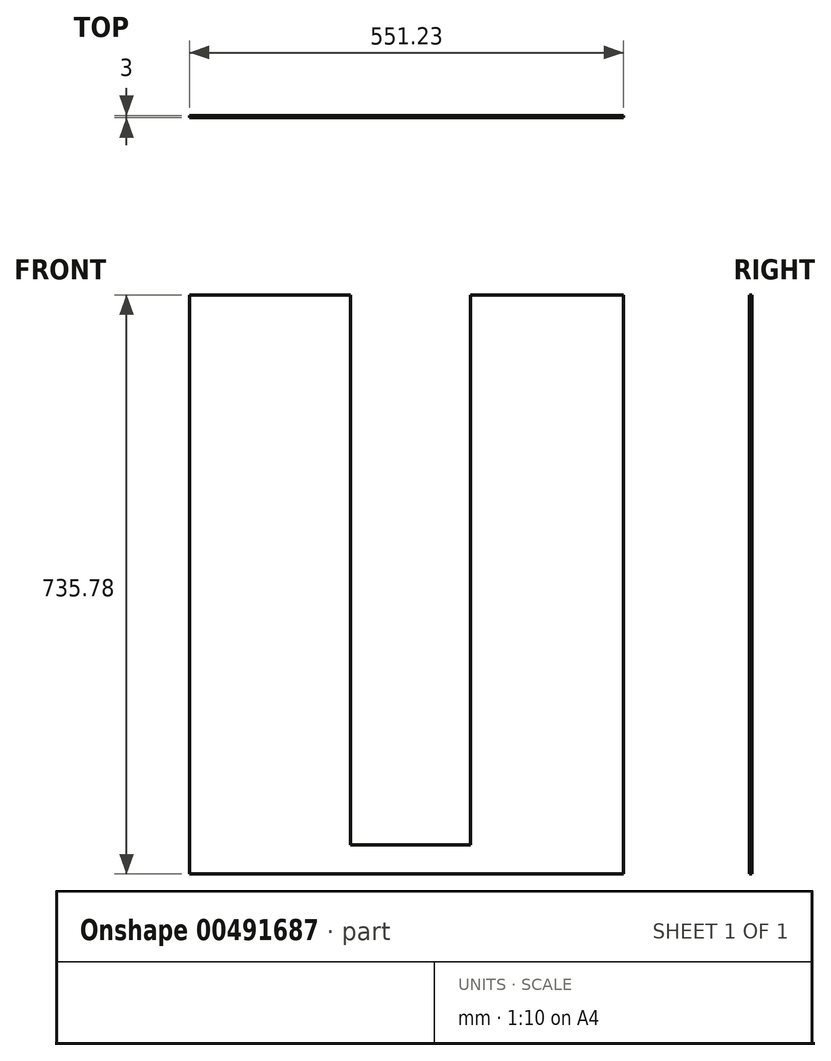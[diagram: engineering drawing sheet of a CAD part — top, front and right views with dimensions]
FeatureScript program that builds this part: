
annotation { "Feature Type Name" : "Feature", "Feature Type Description" : "" }
export const myFeature = defineFeature(function(context is Context, id is Id, definition is map)
    precondition{}
    {
        {
            var Q0;
            Q0=qCreatedBy(makeId("Front.planeOp"),FACE);
            var sketch = newSketch(context, id + "F0", { "sketchPlane" : qUnion([Q0])});
            skLineSegment(sketch, "E0.bottom", {"start": v(-280.6, 698.5) * mm, "end": v(280.6, 698.5) * mm});
            skLineSegment(sketch, "E0.top", {"start": v(-280.6, -41.27) * mm, "end": v(280.6, -41.27) * mm});
            skLineSegment(sketch, "E0.left", {"start": v(-280.6, 698.5) * mm, "end": v(-280.6, -41.27) * mm});
            skLineSegment(sketch, "E0.right", {"start": v(280.6, 698.5) * mm, "end": v(280.6, -41.27) * mm});
            skLineSegment(sketch, "E1", {"start": v(-280.6, 698.5) * mm, "end": v(0, 698.5) * mm});
            skLineSegment(sketch, "E2", {"start": v(0, 698.5) * mm, "end": v(0, 0) * mm});
            skLineSegment(sketch, "E3", {"start": v(0, 698.5) * mm, "end": v(-76.2, 698.5) * mm});
            skLineSegment(sketch, "E4", {"start": v(0, 698.5) * mm, "end": v(76.2, 698.5) * mm});
            skLineSegment(sketch, "E5", {"start": v(-76.2, 698.5) * mm, "end": v(-76.2, 0) * mm});
            skLineSegment(sketch, "E6", {"start": v(76.2, 0) * mm, "end": v(76.2, 698.5) * mm});
            skLineSegment(sketch, "E7", {"start": v(-76.2, 0) * mm, "end": v(76.2, 0) * mm});
            skSolve(sketch);
        }
        {
            var Q0;
            Q0=makeQuery(id+"F0.imprint","IMPRINT",FACE,{"disambiguationData":[TD([[makeQuery(id+"F0.imprint","IMPRINT",EDGE,{"derivedFrom":sQuery(id+"F0.wireOp",EDGE,"E0.bottom")}),-1.0]])]});
            extrude(context, id + "F1", {"entities" : qUnion([Q0]), "depth" : 3 * mm});
        }
        {
            var Q0;
            Q0=makeQuery(id+"F1.opExtrude","CAP_FACE",FACE,{"disambiguationData":[OSD([sQuery(id+"F0.wireOp",EDGE,"E0.bottom"),sQuery(id+"F0.wireOp",EDGE,"E0.top"),sQuery(id+"F0.wireOp",EDGE,"E0.left"),sQuery(id+"F0.wireOp",EDGE,"E0.right"),sQuery(id+"F0.wireOp",EDGE,"E1"),sQuery(id+"F0.wireOp",EDGE,"E5"),sQuery(id+"F0.wireOp",EDGE,"E6"),sQuery(id+"F0.wireOp",EDGE,"E7")])],"isStart":false});
            var sketch = newSketch(context, id + "F2", { "sketchPlane" : qUnion([Q0])});
            skLineSegment(sketch, "E8", {"start": v(-280.6, -41.27) * mm, "end": v(-280.6, -37.27) * mm});
            skLineSegment(sketch, "E9", {"start": v(-280.6, -37.27) * mm, "end": v(280.6, -37.27) * mm});
            skLineSegment(sketch, "E10", {"start": v(280.6, -37.27) * mm, "end": v(280.6, -41.27) * mm});
            skLineSegment(sketch, "E11", {"start": v(280.6, -41.27) * mm, "end": v(-280.24, -41.27) * mm});
            skLineSegment(sketch, "E12", {"start": v(-280.24, -41.27) * mm, "end": v(-280.6, -41.27) * mm});
            skSolve(sketch);
        }
        {
            var Q0;
            Q0=makeQuery(id+"F2.imprint","IMPRINT",FACE,{"disambiguationData":[TD([[makeQuery(id+"F2.imprint","IMPRINT",EDGE,{"derivedFrom":sQuery(id+"F2.wireOp",EDGE,"E8")}),1.0]])]});
            extrude(context, id + "F3", {"entities" : qUnion([Q0]), "operationType" : NewBodyOperationType.REMOVE, "oppositeDirection" : true, "depth" : 25.4 * mm});
        }
        {
            var Q0;
            Q0=makeQuery(id+"F1.opExtrude","CAP_FACE",FACE,{"disambiguationData":[OSD([sQuery(id+"F0.wireOp",EDGE,"E0.bottom"),sQuery(id+"F0.wireOp",EDGE,"E0.top"),sQuery(id+"F0.wireOp",EDGE,"E0.left"),sQuery(id+"F0.wireOp",EDGE,"E0.right"),sQuery(id+"F0.wireOp",EDGE,"E1"),sQuery(id+"F0.wireOp",EDGE,"E5"),sQuery(id+"F0.wireOp",EDGE,"E6"),sQuery(id+"F0.wireOp",EDGE,"E7")])],"isStart":false});
            var sketch = newSketch(context, id + "F4", { "sketchPlane" : qUnion([Q0])});
            skLineSegment(sketch, "E13.bottom", {"start": v(280.6, 698.5) * mm, "end": v(270.64, 698.5) * mm});
            skLineSegment(sketch, "E13.top", {"start": v(280.6, -37.27) * mm, "end": v(270.64, -37.27) * mm});
            skLineSegment(sketch, "E13.left", {"start": v(280.6, 698.5) * mm, "end": v(280.6, -37.27) * mm});
            skLineSegment(sketch, "E13.right", {"start": v(270.64, 698.5) * mm, "end": v(270.64, -37.27) * mm});
            skSolve(sketch);
        }
        {
            var Q0;
            Q0 = qSketchRegion(id + "F4", true);
            extrude(context, id + "F5", {"entities" : qUnion([Q0]), "operationType" : NewBodyOperationType.REMOVE, "oppositeDirection" : true, "depth" : 25.4 * mm});
        }
    });
